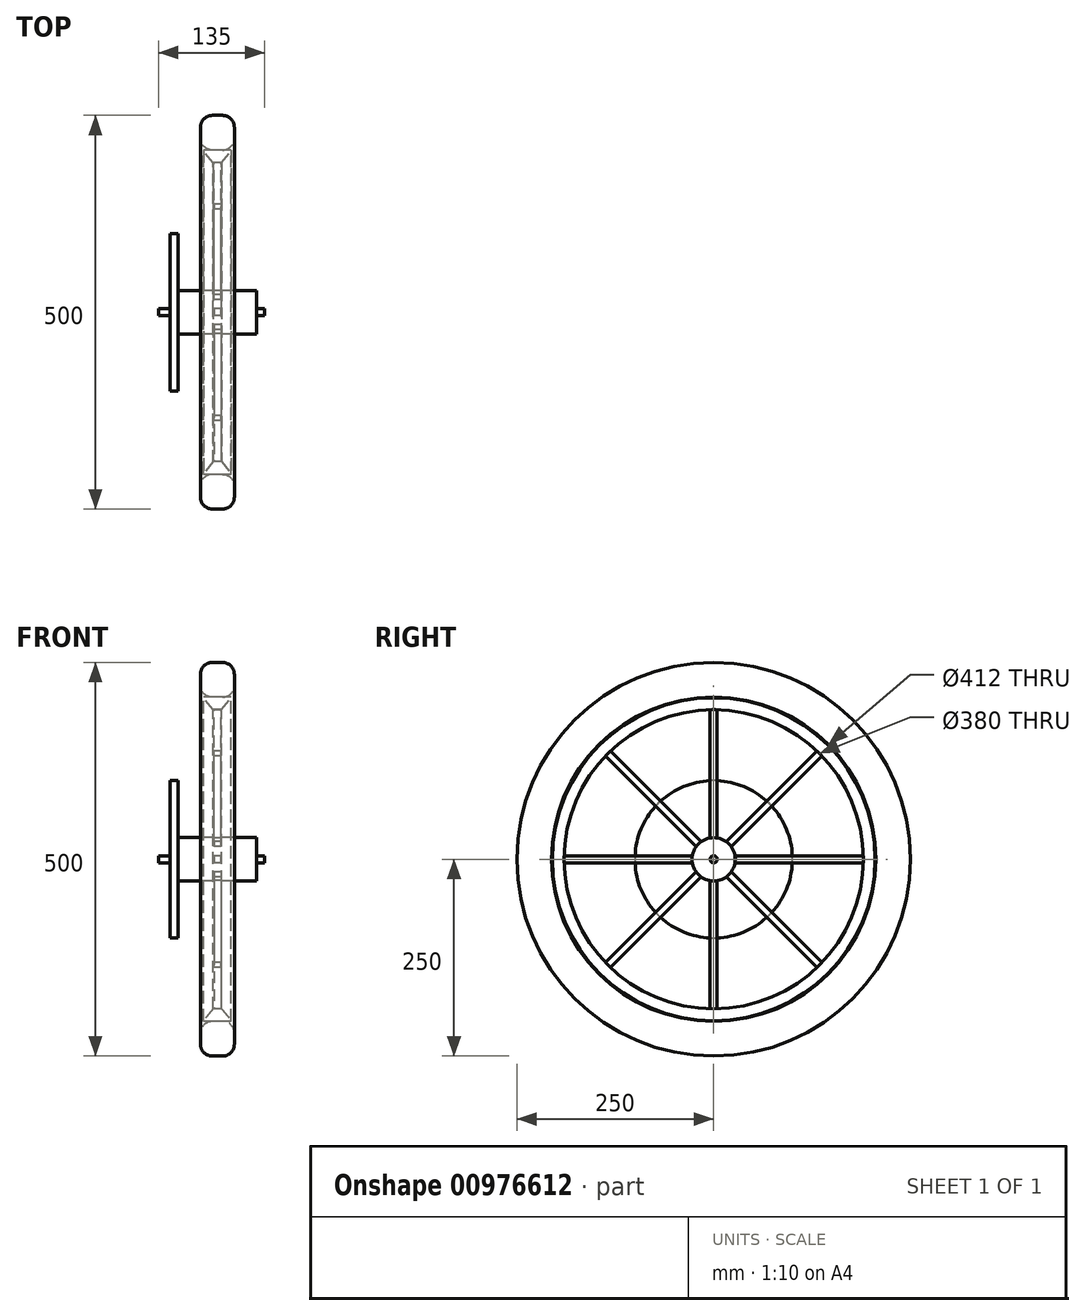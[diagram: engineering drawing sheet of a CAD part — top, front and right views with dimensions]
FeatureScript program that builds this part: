
annotation { "Feature Type Name" : "Feature", "Feature Type Description" : "" }
export const myFeature = defineFeature(function(context is Context, id is Id, definition is map)
    precondition{}
    {
        {
            var Q0;
            Q0=qCreatedBy(makeId("Right.planeOp"),FACE);
            var sketch = newSketch(context, id + "F0", { "sketchPlane" : qUnion([Q0])});
            skCircle(sketch, "E0", {"center": v(0, 0) * mm, "radius": 250 * mm});
            skCircle(sketch, "E1", {"center": v(0, 0) * mm, "radius": 190 * mm});
            skCircle(sketch, "E2", {"center": v(0, 0) * mm, "radius": 206 * mm});
            skCircle(sketch, "E3", {"center": v(0, 0) * mm, "radius": 27.5 * mm});
            skCircle(sketch, "E4", {"center": v(0, 0) * mm, "radius": 4.5 * mm});
            skLineSegment(sketch, "E5.trimOffspring", {"start": v(-16, 22.37) * mm, "end": v(-131.13, 137.5) * mm});
            skLineSegment(sketch, "E6.trimOffspring", {"start": v(-4.5, 27.13) * mm, "end": v(-4.5, 189.95) * mm});
            skLineSegment(sketch, "E7.trimOffspring", {"start": v(4.5, 27.13) * mm, "end": v(4.5, 189.95) * mm});
            skLineSegment(sketch, "E8.trimOffspring", {"start": v(16, 22.37) * mm, "end": v(131.13, 137.5) * mm});
            skLineSegment(sketch, "E9.trimOffspring", {"start": v(22.37, 16) * mm, "end": v(137.5, 131.13) * mm});
            skLineSegment(sketch, "E10.trimOffspring", {"start": v(22.37, -16) * mm, "end": v(137.5, -131.13) * mm});
            skLineSegment(sketch, "E11.trimOffspring", {"start": v(27.13, -4.5) * mm, "end": v(189.95, -4.5) * mm});
            skLineSegment(sketch, "E12.trimOffspring", {"start": v(-27.13, 4.5) * mm, "end": v(-189.95, 4.5) * mm});
            skLineSegment(sketch, "E13.trimOffspring", {"start": v(-22.37, 16) * mm, "end": v(-137.5, 131.13) * mm});
            skLineSegment(sketch, "E14.trimOffspring", {"start": v(-22.37, -16) * mm, "end": v(-137.5, -131.13) * mm});
            skLineSegment(sketch, "E15.trimOffspring", {"start": v(-27.13, -4.5) * mm, "end": v(-189.95, -4.5) * mm});
            skLineSegment(sketch, "E16.trimOffspring", {"start": v(-4.5, -27.13) * mm, "end": v(-4.5, -189.95) * mm});
            skLineSegment(sketch, "E17.trimOffspring", {"start": v(-16, -22.37) * mm, "end": v(-131.13, -137.5) * mm});
            skLineSegment(sketch, "E18.trimOffspring", {"start": v(16, -22.37) * mm, "end": v(131.13, -137.5) * mm});
            skLineSegment(sketch, "E19.trimOffspring", {"start": v(4.5, -27.13) * mm, "end": v(4.5, -189.95) * mm});
            skLineSegment(sketch, "E20", {"start": v(27.16, 4.32) * mm, "end": v(189.95, 4.32) * mm});
            skSolve(sketch);
        }
        {
            var Q0;
            Q0=makeQuery(id+"F0.imprint","IMPRINT",FACE,{"disambiguationData":[TD([[makeQuery(id+"F0.imprint","IMPRINT",EDGE,{"derivedFrom":sQuery(id+"F0.wireOp",EDGE,"E4")}),1.0]])]});
            extrude(context, id + "F1", {"entities" : qUnion([Q0]), "depth" : 120 * mm, "offsetDistance" : 25 * mm, "symmetric" : true});
        }
        {
            var Q0;
            Q0=makeQuery(id+"F0.imprint","IMPRINT",FACE,{"disambiguationData":[TD([[makeQuery(id+"F0.imprint","IMPRINT",EDGE,{"derivedFrom":sQuery(id+"F0.wireOp",EDGE,"E4")}),-1.0]])]});
            extrude(context, id + "F2", {"entities" : qUnion([Q0]), "operationType" : NewBodyOperationType.ADD, "depth" : 100 * mm, "offsetDistance" : 25 * mm, "symmetric" : true});
        }
        {
            var Q0;
            {var subQ0=sQuery(id+"F0.wireOp",EDGE,"E6.trimOffspring");Q0=makeQuery(id+"F0.imprint","IMPRINT",FACE,{"disambiguationData":[TD([[makeQuery(id+"F0.imprint","IMPRINT",EDGE,{"derivedFrom":subQ0}),-1.0]])]});}
            var Q1;
            {var subQ0=sQuery(id+"F0.wireOp",EDGE,"E5.trimOffspring");Q1=makeQuery(id+"F0.imprint","IMPRINT",FACE,{"disambiguationData":[TD([[makeQuery(id+"F0.imprint","IMPRINT",EDGE,{"derivedFrom":subQ0}),1.0]])]});}
            var Q2;
            {var subQ0=sQuery(id+"F0.wireOp",EDGE,"E12.trimOffspring");Q2=makeQuery(id+"F0.imprint","IMPRINT",FACE,{"disambiguationData":[TD([[makeQuery(id+"F0.imprint","IMPRINT",EDGE,{"derivedFrom":subQ0}),1.0]])]});}
            var Q3;
            {var subQ0=sQuery(id+"F0.wireOp",EDGE,"E14.trimOffspring");Q3=makeQuery(id+"F0.imprint","IMPRINT",FACE,{"disambiguationData":[TD([[makeQuery(id+"F0.imprint","IMPRINT",EDGE,{"derivedFrom":subQ0}),1.0]])]});}
            var Q4;
            {var subQ0=sQuery(id+"F0.wireOp",EDGE,"E8.trimOffspring");Q4=makeQuery(id+"F0.imprint","IMPRINT",FACE,{"disambiguationData":[TD([[makeQuery(id+"F0.imprint","IMPRINT",EDGE,{"derivedFrom":subQ0}),-1.0]])]});}
            var Q5;
            {var subQ0=sQuery(id+"F0.wireOp",EDGE,"67cea25c-e70a-43c1-b273-0d9cde0979ee.trimOffspring");Q5=makeQuery(id+"F0.imprint","IMPRINT",FACE,{"disambiguationData":[TD([[makeQuery(id+"F0.imprint","IMPRINT",EDGE,{"derivedFrom":subQ0}),-1.0]])]});}
            var Q6;
            {var subQ0=sQuery(id+"F0.wireOp",EDGE,"E10.trimOffspring");Q6=makeQuery(id+"F0.imprint","IMPRINT",FACE,{"disambiguationData":[TD([[makeQuery(id+"F0.imprint","IMPRINT",EDGE,{"derivedFrom":subQ0}),-1.0]])]});}
            var Q7;
            {var subQ0=sQuery(id+"F0.wireOp",EDGE,"E16.trimOffspring");Q7=makeQuery(id+"F0.imprint","IMPRINT",FACE,{"disambiguationData":[TD([[makeQuery(id+"F0.imprint","IMPRINT",EDGE,{"derivedFrom":subQ0}),1.0]])]});}
            var Q8;
            {var subQ0=sQuery(id+"F0.wireOp",EDGE,"E11.trimOffspring");Q8=makeQuery(id+"F0.imprint","IMPRINT",FACE,{"disambiguationData":[TD([[makeQuery(id+"F0.imprint","IMPRINT",EDGE,{"derivedFrom":subQ0}),1.0]])]});}
            extrude(context, id + "F3", {"entities" : qUnion([Q0, Q1, Q2, Q3, Q4, Q5, Q6, Q7, Q8]), "operationType" : NewBodyOperationType.ADD, "depth" : 9 * mm, "offsetDistance" : 25 * mm, "symmetric" : true});
        }
        {
            var Q0;
            Q0=makeQuery(id+"F0.imprint","IMPRINT",FACE,{"disambiguationData":[TD([[makeQuery(id+"F0.imprint","IMPRINT",EDGE,{"derivedFrom":sQuery(id+"F0.wireOp",EDGE,"E0")}),1.0]])]});
            extrude(context, id + "F4", {"entities" : qUnion([Q0]), "depth" : 43 * mm, "offsetDistance" : 25 * mm, "symmetric" : true});
        }
        {
            var Q0;
            Q0=makeQuery(id+"F0.imprint","IMPRINT",FACE,{"disambiguationData":[TD([[makeQuery(id+"F0.imprint","IMPRINT",EDGE,{"derivedFrom":sQuery(id+"F0.wireOp",EDGE,"E2")}),1.0]])]});
            extrude(context, id + "F5", {"entities" : qUnion([Q0]), "depth" : 35 * mm, "offsetDistance" : 25 * mm, "symmetric" : true});
        }
        {
            var Q0;
            Q0=makeQuery(id+"F4.opExtrude","SWEPT_FACE",FACE,{"disambiguationData":[OSD([sQuery(id+"F0.wireOp",EDGE,"E0")])]});
            var Q1;
            Q1=makeQuery(id+"F4.opExtrude","CAP_FACE",FACE,{"disambiguationData":[OSD([sQuery(id+"F0.wireOp",EDGE,"E0"),sQuery(id+"F0.wireOp",EDGE,"E2")])],"isStart":true});
            var Q2;
            Q2=makeQuery(id+"F4.opExtrude","CAP_FACE",FACE,{"disambiguationData":[OSD([sQuery(id+"F0.wireOp",EDGE,"E0"),sQuery(id+"F0.wireOp",EDGE,"E2")])],"isStart":false});
            fillet(context, id + "F6", {"entities" : qUnion([Q0, Q1, Q2]), "radius" : 15 * mm, "tangentPropagation" : true, "allowEdgeOverflow" : false});
        }
        {
            var Q0;
            Q0=makeQuery(id+"F5.opExtrude","CAP_EDGE",EDGE,{"disambiguationData":[OSD([sQuery(id+"F0.wireOp",EDGE,"E1")])],"isStart":false});
            var Q1;
            Q1=makeQuery(id+"F5.opExtrude","CAP_EDGE",EDGE,{"disambiguationData":[OSD([sQuery(id+"F0.wireOp",EDGE,"E1")])],"isStart":true});
            chamfer(context, id + "F7", {"entities" : qUnion([Q0, Q1]), "chamferType" : ChamferType.TWO_OFFSETS, "width1" : 12 * mm, "oppositeDirection" : false, "width2" : 15 * mm, "tangentPropagation" : true});
        }
        {
            var Q0;
            Q0=makeQuery(id+"F2.opExtrude","CAP_FACE",FACE,{"disambiguationData":[OSD([sQuery(id+"F0.wireOp",EDGE,"E3"),sQuery(id+"F0.wireOp",EDGE,"E4")])],"isStart":true});
            var sketch = newSketch(context, id + "F8", { "sketchPlane" : qUnion([Q0])});
            skCircle(sketch, "E21", {"center": v(0, 0) * mm, "radius": 100 * mm});
            skSolve(sketch);
        }
        {
            var Q0;
            Q0=qSketchRegion(id+"F8",true);
            extrude(context, id + "F9", {"entities" : qUnion([Q0]), "operationType" : NewBodyOperationType.ADD, "depth" : 10 * mm, "offsetDistance" : 25 * mm});
        }
        {
            var Q0;
            Q0=makeQuery(id+"F9.boolean.opBoolean","MERGE",FACE,{"derivedFrom":[makeQuery(id+"F1.opExtrude","CAP_FACE",FACE,{"disambiguationData":[OSD([sQuery(id+"F0.wireOp",EDGE,"E4")])],"isStart":true}),makeQuery(id+"F9.opExtrude","CAP_FACE",FACE,{"disambiguationData":[OSD([sQuery(id+"F8.wireOp",EDGE,"E21")])],"isStart":false})]});
            var sketch = newSketch(context, id + "F10", { "sketchPlane" : qUnion([Q0])});
            skCircle(sketch, "E22", {"center": v(0, 0) * mm, "radius": 4.5 * mm});
            skSolve(sketch);
        }
        {
            var Q0;
            Q0=makeQuery(id+"F10.imprint","IMPRINT",FACE,{"disambiguationData":[TD([[makeQuery(id+"F10.imprint","IMPRINT",EDGE,{"derivedFrom":sQuery(id+"F10.wireOp",EDGE,"E22")}),1.0]])]});
            extrude(context, id + "F11", {"entities" : qUnion([Q0]), "operationType" : NewBodyOperationType.ADD, "depth" : 15 * mm, "offsetDistance" : 25 * mm});
        }
    });
